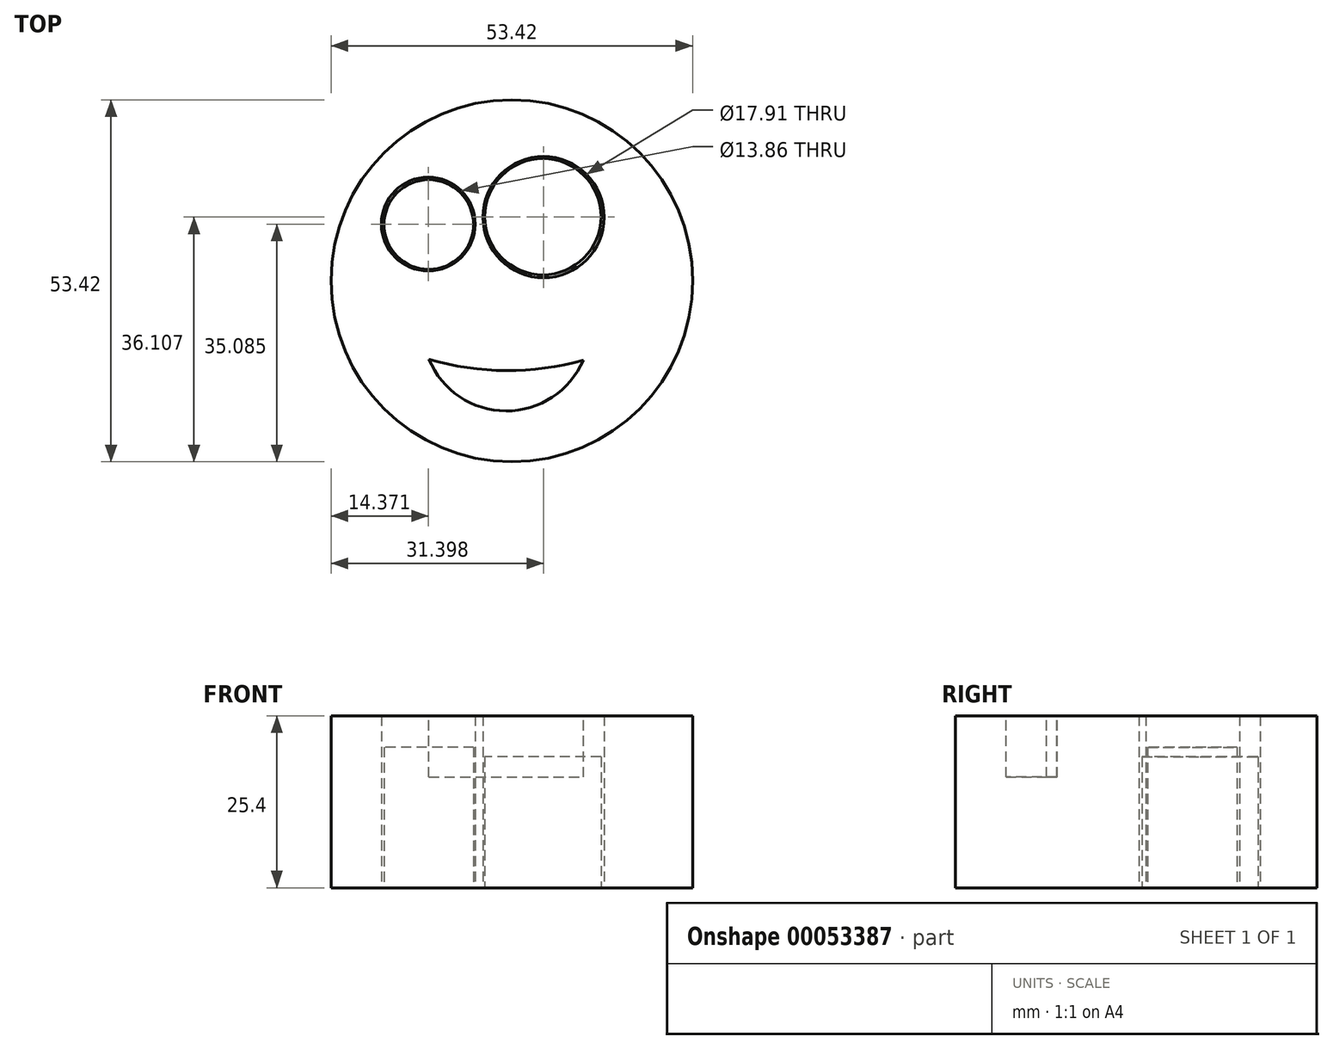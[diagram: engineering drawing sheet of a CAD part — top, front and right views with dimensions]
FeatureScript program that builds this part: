
annotation { "Feature Type Name" : "Feature", "Feature Type Description" : "" }
export const myFeature = defineFeature(function(context is Context, id is Id, definition is map)
    precondition{}
    {
        {
            var Q0;
            Q0=qCreatedBy(makeId("Top.planeOp"),FACE);
            var sketch = newSketch(context, id + "F0", { "sketchPlane" : qUnion([Q0])});
            skCircle(sketch, "E0", {"center": v(-50.2, -15.35) * mm, "radius": 26.7 * mm});
            skSolve(sketch);
        }
        {
            var Q0;
            Q0=makeQuery(id+"F0.imprint","IMPRINT",FACE,{"disambiguationData":[TD([[makeQuery(id+"F0.imprint","IMPRINT",EDGE,{"derivedFrom":sQuery(id+"F0.wireOp",EDGE,"E0")}),1.0]])]});
            var sketch = newSketch(context, id + "F1", { "sketchPlane" : qUnion([Q0])});
            skCircle(sketch, "E1", {"center": v(-62.54, -6.98) * mm, "radius": 6.93 * mm});
            skCircle(sketch, "E2", {"center": v(-45.51, -5.95) * mm, "radius": 8.95 * mm});
            skSolve(sketch);
        }
        {
            var Q0;
            Q0=makeQuery(id+"F1.imprint","IMPRINT",FACE,{"disambiguationData":[TD([[makeQuery(id+"F1.imprint","IMPRINT",EDGE,{"derivedFrom":sQuery(id+"F1.wireOp",EDGE,"E1")}),-1.0]])]});
            extrude(context, id + "F2", {"entities" : qUnion([Q0]), "depth" : 25.4 * mm});
        }
        {
            var Q0;
            Q0=makeQuery(id+"F0.imprint","IMPRINT",FACE,{"disambiguationData":[TD([[makeQuery(id+"F0.imprint","IMPRINT",EDGE,{"derivedFrom":sQuery(id+"F0.wireOp",EDGE,"E0")}),1.0]])]});
            var sketch = newSketch(context, id + "F3", { "sketchPlane" : qUnion([Q0])});
            skCircle(sketch, "E3", {"center": v(-62.47, -7.04) * mm, "radius": 6.61 * mm});
            skCircle(sketch, "E4", {"center": v(-45.61, -6.35) * mm, "radius": 8.71 * mm});
            skSolve(sketch);
        }
        {
            var Q0;
            Q0=makeQuery(id+"F2.opExtrude","CAP_FACE",FACE,{"disambiguationData":[OSD([sQuery(id+"F0.wireOp",EDGE,"E0"),sQuery(id+"F1.wireOp",EDGE,"E1"),sQuery(id+"F1.wireOp",EDGE,"E2")])],"isStart":false});
            var sketch = newSketch(context, id + "F4", { "sketchPlane" : qUnion([Q0])});
            skArc(sketch, "E5", {"start": v(-62.44, -26.95) * mm, "mid": v(-51.07, -34.57) * mm, "end": v(-39.64, -27.06) * mm});
            skArc(sketch, "E6", {"start": v(-62.44, -26.95) * mm, "mid": v(-51.05, -28.6) * mm, "end": v(-39.64, -27.06) * mm});
            skSolve(sketch);
        }
        {
            var Q0;
            Q0=makeQuery(id+"F4.imprint","IMPRINT",FACE,{"disambiguationData":[TD([[makeQuery(id+"F4.imprint","IMPRINT",EDGE,{"derivedFrom":sQuery(id+"F4.wireOp",EDGE,"E5")}),1.0]])]});
            extrude(context, id + "F5", {"entities" : qUnion([Q0]), "operationType" : NewBodyOperationType.REMOVE, "oppositeDirection" : true, "depth" : 9.07 * mm});
        }
        {
            var Q0;
            Q0=makeQuery(id+"F3.imprint","IMPRINT",FACE,{"disambiguationData":[TD([[makeQuery(id+"F3.imprint","IMPRINT",EDGE,{"derivedFrom":sQuery(id+"F3.wireOp",EDGE,"E3")}),1.0]])]});
            extrude(context, id + "F6", {"entities" : qUnion([Q0]), "depth" : 20.76 * mm});
        }
        {
            var Q0;
            Q0=makeQuery(id+"F0.imprint","IMPRINT",FACE,{"disambiguationData":[TD([[makeQuery(id+"F0.imprint","IMPRINT",EDGE,{"derivedFrom":sQuery(id+"F0.wireOp",EDGE,"E0")}),1.0]])]});
            var sketch = newSketch(context, id + "F7", { "sketchPlane" : qUnion([Q0])});
            skCircle(sketch, "E7", {"center": v(-45.61, -5.89) * mm, "radius": 8.58 * mm});
            skSolve(sketch);
        }
        {
            var Q0;
            Q0=makeQuery(id+"F7.imprint","IMPRINT",FACE,{"disambiguationData":[TD([[makeQuery(id+"F7.imprint","IMPRINT",EDGE,{"derivedFrom":sQuery(id+"F7.wireOp",EDGE,"E7")}),1.0]])]});
            extrude(context, id + "F8", {"entities" : qUnion([Q0]), "depth" : 19.34 * mm});
        }
    });
